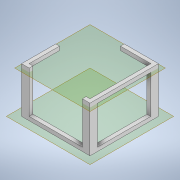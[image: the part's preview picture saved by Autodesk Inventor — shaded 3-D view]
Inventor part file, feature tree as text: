
AUTODESK INVENTOR PART (.ipt)
format: ipt  version: 2022 (Build 260153000, 153)  size: 171,520 bytes
history: native  units: in
note: dims shown in document units (in); Inventor stores cm internally (conversion verified against a paired STEP export)
features: extrude x3, sketch x3, plane x2
ambient origin geometry x8: Origin, YZ Plane, XZ Plane, XY Plane, X Axis, Y Axis, Z Axis, Center Point
bodies: Solid1 (feature_tree)
feature tree (8):
  extrude  "Extrusion1"  Depth=0.7087in
  plane  "Work Plane1"
  plane  "Work Plane6"
  extrude  "Extrusion5"  Depth=0.6299in
  extrude  "Extrusion6"  Depth=0.0394in
  sketch  "Sketch1"  dims[d4=0.7087in d5=0.7087in]
  sketch  "Sketch11"  dims[d10=0.6299in d11=0.6299in]
  sketch  "Sketch12"  dims[d12=0.0394in d13=0.0in d33=0.0394in d53=0.0in d54=0.0787in d55=0.0394in d56=0.0787in d57=0.0394in d58=0.3937in d59=0.0in d60=0.0394in d61=0.0in d62=0.0394in d63=0.0394in]
